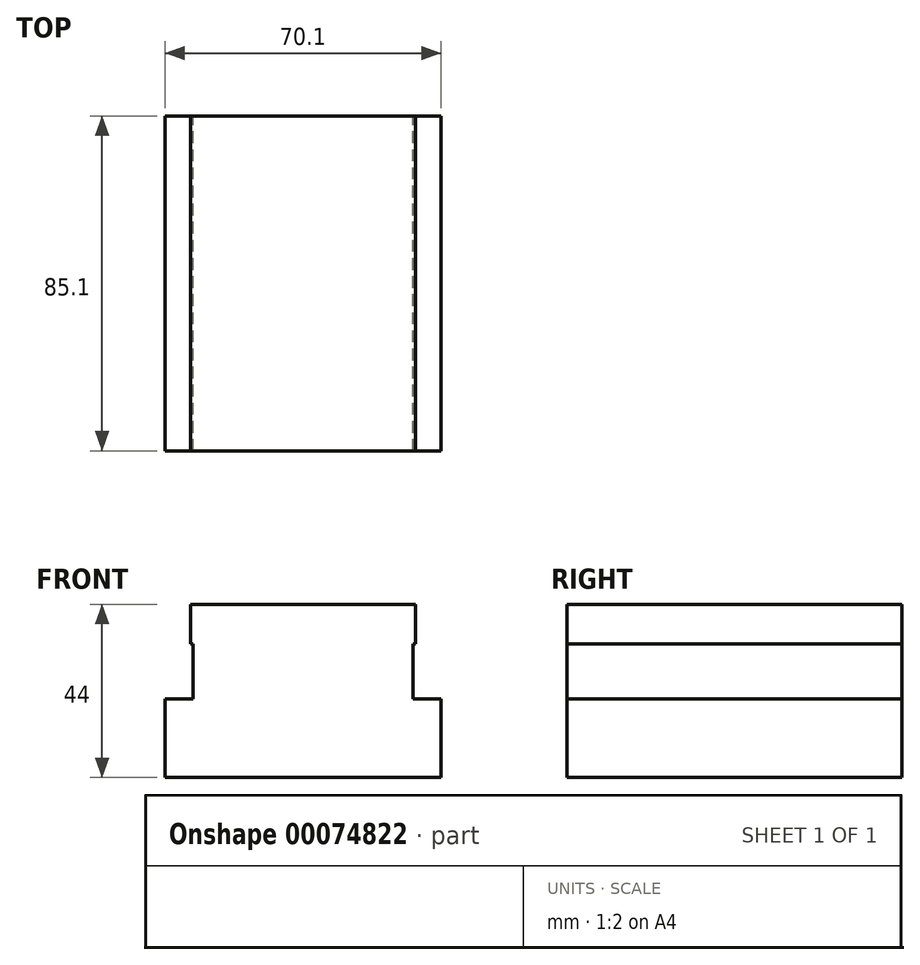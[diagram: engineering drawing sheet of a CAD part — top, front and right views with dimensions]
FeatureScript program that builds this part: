
annotation { "Feature Type Name" : "Feature", "Feature Type Description" : "" }
export const myFeature = defineFeature(function(context is Context, id is Id, definition is map)
    precondition{}
    {
        {
            var Q0;
            Q0=qCreatedBy(makeId("Top.planeOp"),FACE);
            var sketch = newSketch(context, id + "F0", { "sketchPlane" : qUnion([Q0])});
            skLineSegment(sketch, "E0.bottom", {"start": v(-35.05, -42.55) * mm, "end": v(35.05, -42.55) * mm});
            skLineSegment(sketch, "E0.top", {"start": v(-35.05, 42.55) * mm, "end": v(35.05, 42.55) * mm});
            skLineSegment(sketch, "E0.left", {"start": v(-35.05, -42.55) * mm, "end": v(-35.05, 42.55) * mm});
            skLineSegment(sketch, "E0.right", {"start": v(35.05, -42.55) * mm, "end": v(35.05, 42.55) * mm});
            skLineSegment(sketch, "E1", {"start": v(0, 42.55) * mm, "end": v(0, -42.55) * mm, "construction": true});
            skSolve(sketch);
        }
        {
            var Q0;
            Q0=qSketchRegion(id+"F0",true);
            extrude(context, id + "F1", {"entities" : qUnion([Q0]), "endBound" : BoundingType.SYMMETRIC, "depth" : 20 * mm});
        }
        {
            var Q0;
            Q0=makeQuery(id+"F1.opExtrude","CAP_FACE",FACE,{"disambiguationData":[OSD([sQuery(id+"F0.wireOp",EDGE,"E0.bottom"),sQuery(id+"F0.wireOp",EDGE,"E0.top"),sQuery(id+"F0.wireOp",EDGE,"E0.left"),sQuery(id+"F0.wireOp",EDGE,"E0.right")])],"isStart":false});
            var sketch = newSketch(context, id + "F2", { "sketchPlane" : qUnion([Q0])});
            skLineSegment(sketch, "E2.bottom", {"start": v(-27.94, -42.55) * mm, "end": v(27.94, -42.55) * mm});
            skLineSegment(sketch, "E2.top", {"start": v(-27.94, 42.55) * mm, "end": v(27.94, 42.55) * mm});
            skLineSegment(sketch, "E2.left", {"start": v(-27.94, -42.55) * mm, "end": v(-27.94, 42.55) * mm});
            skLineSegment(sketch, "E2.right", {"start": v(27.94, -42.55) * mm, "end": v(27.94, 42.55) * mm});
            skLineSegment(sketch, "E3", {"start": v(0, -42.55) * mm, "end": v(0, 42.55) * mm, "construction": true});
            skSolve(sketch);
        }
        {
            var Q0;
            Q0=qSketchRegion(id+"F2",true);
            extrude(context, id + "F3", {"entities" : qUnion([Q0]), "operationType" : NewBodyOperationType.ADD, "depth" : 14 * mm});
        }
        {
            var Q0;
            Q0=makeQuery(id+"F3.opExtrude","CAP_FACE",FACE,{"disambiguationData":[OSD([sQuery(id+"F2.wireOp",EDGE,"E2.bottom"),sQuery(id+"F2.wireOp",EDGE,"E2.top"),sQuery(id+"F2.wireOp",EDGE,"E2.left"),sQuery(id+"F2.wireOp",EDGE,"E2.right")])],"isStart":false});
            var sketch = newSketch(context, id + "F4", { "sketchPlane" : qUnion([Q0])});
            skLineSegment(sketch, "E4.bottom", {"start": v(-28.58, 42.55) * mm, "end": v(28.58, 42.55) * mm});
            skLineSegment(sketch, "E4.top", {"start": v(-28.58, -42.55) * mm, "end": v(28.58, -42.55) * mm});
            skLineSegment(sketch, "E4.left", {"start": v(-28.57, 42.54) * mm, "end": v(-28.58, -42.54) * mm});
            skLineSegment(sketch, "E4.right", {"start": v(28.58, 42.55) * mm, "end": v(28.57, -42.55) * mm});
            skLineSegment(sketch, "E5", {"start": v(0, 42.55) * mm, "end": v(0, -42.55) * mm, "construction": true});
            skSolve(sketch);
        }
        {
            var Q0;
            Q0=qSketchRegion(id+"F4",true);
            extrude(context, id + "F5", {"entities" : qUnion([Q0]), "operationType" : NewBodyOperationType.ADD, "depth" : 10 * mm});
        }
    });
